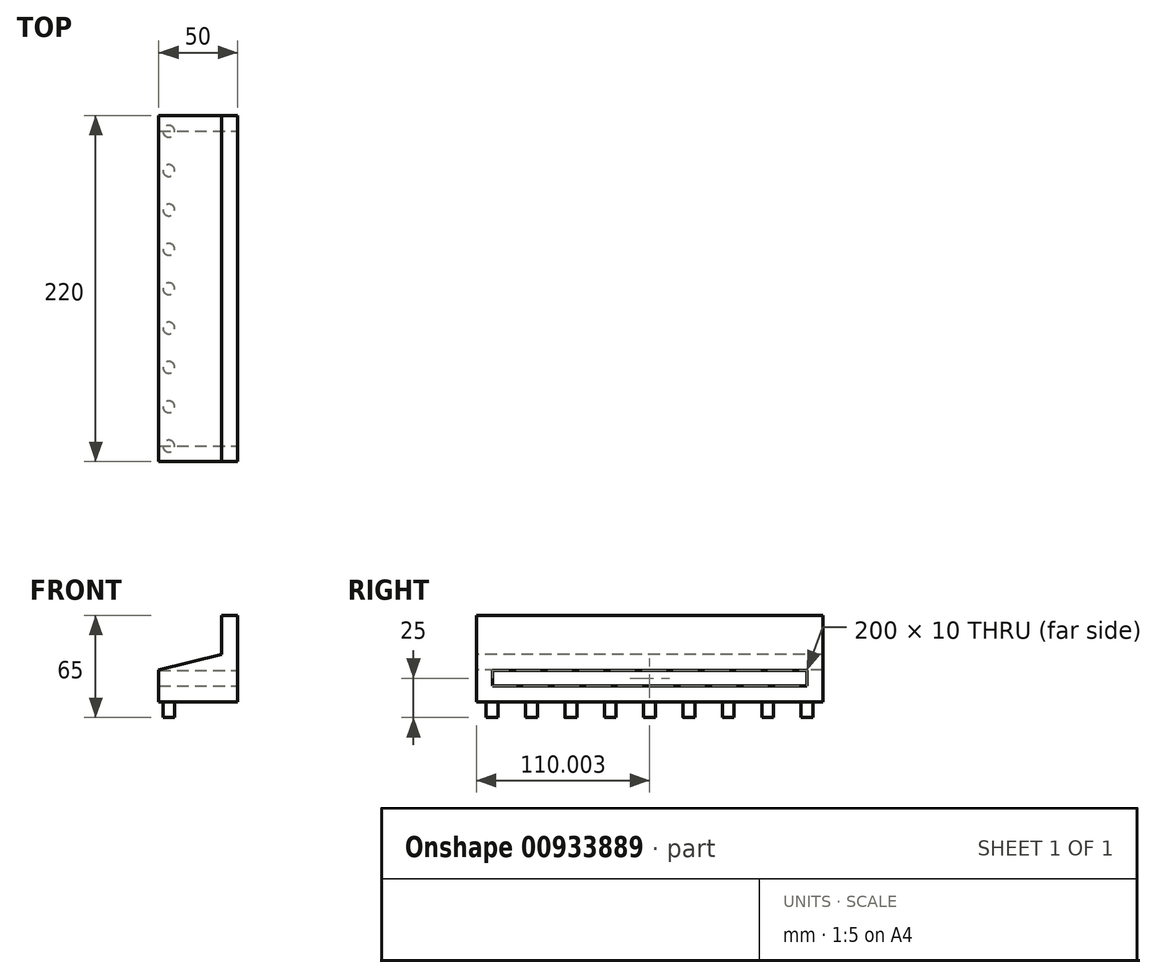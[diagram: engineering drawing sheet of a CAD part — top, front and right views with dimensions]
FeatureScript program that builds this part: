
annotation { "Feature Type Name" : "Feature", "Feature Type Description" : "" }
export const myFeature = defineFeature(function(context is Context, id is Id, definition is map)
    precondition{}
    {
        {
            var Q0;
            Q0=qCreatedBy(makeId("Top.planeOp"),FACE);
            var sketch = newSketch(context, id + "F0", { "sketchPlane" : qUnion([Q0])});
            skLineSegment(sketch, "E0.bottom", {"start": v(-63.16, 118.38) * mm, "end": v(-13.16, 118.38) * mm});
            skLineSegment(sketch, "E0.top", {"start": v(-63.16, -101.62) * mm, "end": v(-13.16, -101.62) * mm});
            skLineSegment(sketch, "E0.left", {"start": v(-63.16, 118.38) * mm, "end": v(-63.16, -101.62) * mm});
            skLineSegment(sketch, "E0.right", {"start": v(-13.16, 118.38) * mm, "end": v(-13.16, -101.62) * mm});
            skSolve(sketch);
        }
        {
            var Q0;
            Q0=makeQuery(id+"F0.imprint","IMPRINT",FACE,{"disambiguationData":[TD([[makeQuery(id+"F0.imprint","IMPRINT",EDGE,{"derivedFrom":sQuery(id+"F0.wireOp",EDGE,"E0.bottom")}),-1.0]])]});
            extrude(context, id + "F1", {"entities" : qUnion([Q0]), "depth" : 30 * mm, "offsetDistance" : 25 * mm});
        }
        {
            var Q0;
            Q0=makeQuery(id+"F1.opExtrude","SWEPT_FACE",FACE,{"disambiguationData":[OSD([sQuery(id+"F0.wireOp",EDGE,"E0.right")])]});
            var sketch = newSketch(context, id + "F2", { "sketchPlane" : qUnion([Q0])});
            skLineSegment(sketch, "E1.bottom", {"start": v(-91.62, 20) * mm, "end": v(108.38, 20) * mm});
            skLineSegment(sketch, "E1.top", {"start": v(-91.62, 10) * mm, "end": v(108.38, 10) * mm});
            skLineSegment(sketch, "E1.right", {"start": v(108.38, 20) * mm, "end": v(108.38, 10) * mm});
            skPoint(sketch, "E1.middle", {"position": v(0, 15) * mm});
            skPoint(sketch, "E1.middle.positionSnap0", {"position": v(-101.62, 15) * mm});
            skPoint(sketch, "E1.centerSnap0", {"position": v(-101.62, 15) * mm});
            skLineSegment(sketch, "E2", {"start": v(-91.62, 20) * mm, "end": v(-91.62, 10) * mm});
            skPoint(sketch, "E1.left.end.orphan", {"position": v(-108.38, 10) * mm});
            skPoint(sketch, "E1.left.start.orphan", {"position": v(-108.38, 20) * mm});
            skSolve(sketch);
        }
        {
            var Q0;
            Q0=makeQuery(id+"F2.imprint","IMPRINT",FACE,{"disambiguationData":[TD([[makeQuery(id+"F2.imprint","IMPRINT",EDGE,{"derivedFrom":sQuery(id+"F2.wireOp",EDGE,"E1.bottom")}),-1.0]])]});
            extrude(context, id + "F3", {"entities" : qUnion([Q0]), "operationType" : NewBodyOperationType.REMOVE, "endBound" : BoundingType.UP_TO_NEXT, "oppositeDirection" : true, "depth" : 25 * mm, "offsetDistance" : 25 * mm});
        }
        {
            var Q0;
            Q0=makeQuery(id+"F1.opExtrude","SWEPT_FACE",FACE,{"disambiguationData":[OSD([sQuery(id+"F0.wireOp",EDGE,"E0.top")])]});
            var sketch = newSketch(context, id + "F4", { "sketchPlane" : qUnion([Q0])});
            skLineSegment(sketch, "E3", {"start": v(-63.16, 20.32) * mm, "end": v(-23.2, 30) * mm});
            skSolve(sketch);
        }
        {
            var Q0;
            {var subQ0=sQuery(id+"F4.wireOp",EDGE,"E3");Q0=makeQuery(id+"F4.imprint","IMPRINT",FACE,{"disambiguationData":[TD([[makeQuery(id+"F4.imprint","IMPRINT",EDGE,{"derivedFrom":subQ0}),1.0]])]});}
            extrude(context, id + "F5", {"entities" : qUnion([Q0]), "operationType" : NewBodyOperationType.REMOVE, "endBound" : BoundingType.UP_TO_NEXT, "oppositeDirection" : true, "depth" : 25 * mm, "offsetDistance" : 25 * mm});
        }
        {
            var Q0;
            Q0=makeQuery(id+"F1.opExtrude","CAP_FACE",FACE,{"disambiguationData":[OSD([sQuery(id+"F0.wireOp",EDGE,"E0.bottom"),sQuery(id+"F0.wireOp",EDGE,"E0.top"),sQuery(id+"F0.wireOp",EDGE,"E0.left"),sQuery(id+"F0.wireOp",EDGE,"E0.right")])],"isStart":false});
            extrude(context, id + "F6", {"entities" : qUnion([Q0]), "operationType" : NewBodyOperationType.ADD, "depth" : 25 * mm, "offsetDistance" : 25 * mm});
        }
        {
            var Q0;
            Q0=makeQuery(id+"F1.opExtrude","CAP_FACE",FACE,{"disambiguationData":[OSD([sQuery(id+"F0.wireOp",EDGE,"E0.bottom"),sQuery(id+"F0.wireOp",EDGE,"E0.top"),sQuery(id+"F0.wireOp",EDGE,"E0.left"),sQuery(id+"F0.wireOp",EDGE,"E0.right")])],"isStart":true});
            var sketch = newSketch(context, id + "F7", { "sketchPlane" : qUnion([Q0])});
            skCircle(sketch, "E4", {"center": v(-56.79, -108.3) * mm, "radius": 3.75 * mm});
            skCircle(sketch, "E5.0.1.0", {"center": v(-56.79, -83.3) * mm, "radius": 3.75 * mm});
            skCircle(sketch, "E5.0.2.0", {"center": v(-56.79, -58.3) * mm, "radius": 3.75 * mm});
            skCircle(sketch, "E5.0.3.0", {"center": v(-56.79, -33.3) * mm, "radius": 3.75 * mm});
            skCircle(sketch, "E5.0.4.0", {"center": v(-56.79, -8.3) * mm, "radius": 3.75 * mm});
            skCircle(sketch, "E5.0.5.0", {"center": v(-56.79, 16.7) * mm, "radius": 3.75 * mm});
            skCircle(sketch, "E5.0.6.0", {"center": v(-56.79, 41.7) * mm, "radius": 3.75 * mm});
            skCircle(sketch, "E5.0.7.0", {"center": v(-56.79, 66.7) * mm, "radius": 3.75 * mm});
            skCircle(sketch, "E5.0.8.0", {"center": v(-56.79, 91.7) * mm, "radius": 3.75 * mm});
            skLineSegment(sketch, "E5.direction1", {"start": v(-56.79, -108.3) * mm, "end": v(-31.79, -108.3) * mm, "construction": true});
            skLineSegment(sketch, "E5.direction2", {"start": v(-56.79, -108.3) * mm, "end": v(-56.79, -83.3) * mm, "construction": true});
            skSolve(sketch);
        }
        {
            var Q0;
            Q0=makeQuery(id+"F7.imprint","IMPRINT",FACE,{"disambiguationData":[TD([[makeQuery(id+"F7.imprint","IMPRINT",EDGE,{"derivedFrom":sQuery(id+"F7.wireOp",EDGE,"E4")}),1.0]])]});
            var Q1;
            Q1=makeQuery(id+"F7.imprint","IMPRINT",FACE,{"disambiguationData":[TD([[makeQuery(id+"F7.imprint","IMPRINT",EDGE,{"derivedFrom":sQuery(id+"F7.wireOp",EDGE,"E5.0.1.0")}),1.0]])]});
            var Q2;
            Q2=makeQuery(id+"F7.imprint","IMPRINT",FACE,{"disambiguationData":[TD([[makeQuery(id+"F7.imprint","IMPRINT",EDGE,{"derivedFrom":sQuery(id+"F7.wireOp",EDGE,"E5.0.2.0")}),1.0]])]});
            var Q3;
            Q3=makeQuery(id+"F7.imprint","IMPRINT",FACE,{"disambiguationData":[TD([[makeQuery(id+"F7.imprint","IMPRINT",EDGE,{"derivedFrom":sQuery(id+"F7.wireOp",EDGE,"E5.0.3.0")}),1.0]])]});
            var Q4;
            Q4=makeQuery(id+"F7.imprint","IMPRINT",FACE,{"disambiguationData":[TD([[makeQuery(id+"F7.imprint","IMPRINT",EDGE,{"derivedFrom":sQuery(id+"F7.wireOp",EDGE,"E5.0.4.0")}),1.0]])]});
            var Q5;
            Q5=makeQuery(id+"F7.imprint","IMPRINT",FACE,{"disambiguationData":[TD([[makeQuery(id+"F7.imprint","IMPRINT",EDGE,{"derivedFrom":sQuery(id+"F7.wireOp",EDGE,"E5.0.5.0")}),1.0]])]});
            var Q6;
            Q6=makeQuery(id+"F7.imprint","IMPRINT",FACE,{"disambiguationData":[TD([[makeQuery(id+"F7.imprint","IMPRINT",EDGE,{"derivedFrom":sQuery(id+"F7.wireOp",EDGE,"E5.0.6.0")}),1.0]])]});
            var Q7;
            Q7=makeQuery(id+"F7.imprint","IMPRINT",FACE,{"disambiguationData":[TD([[makeQuery(id+"F7.imprint","IMPRINT",EDGE,{"derivedFrom":sQuery(id+"F7.wireOp",EDGE,"E5.0.7.0")}),1.0]])]});
            var Q8;
            Q8=makeQuery(id+"F7.imprint","IMPRINT",FACE,{"disambiguationData":[TD([[makeQuery(id+"F7.imprint","IMPRINT",EDGE,{"derivedFrom":sQuery(id+"F7.wireOp",EDGE,"E5.0.8.0")}),1.0]])]});
            extrude(context, id + "F8", {"entities" : qUnion([Q0, Q1, Q2, Q3, Q4, Q5, Q6, Q7, Q8]), "operationType" : NewBodyOperationType.ADD, "depth" : 10 * mm, "offsetDistance" : 25 * mm});
        }
    });
